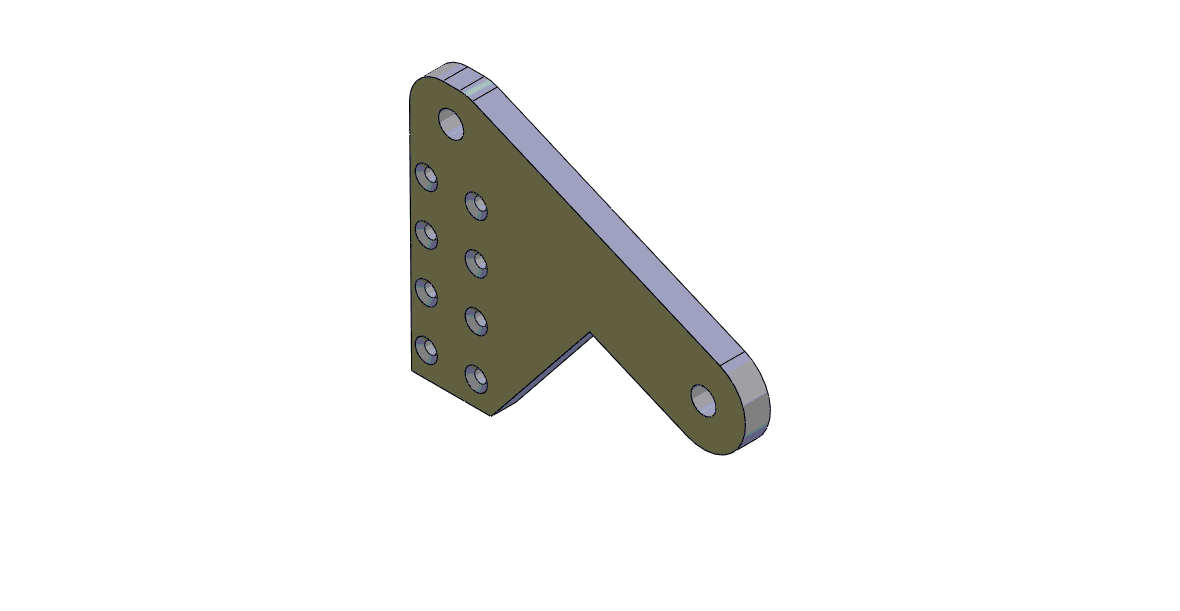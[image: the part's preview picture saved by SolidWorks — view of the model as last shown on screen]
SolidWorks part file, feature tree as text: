
SOLIDWORKS PART (.sldprt)
format: sldprt  version: not decoded by parser v0  size: 235,520 bytes
history: native  units: mm
features: sketch x5, hole x2, material x1, extrude x1 (+13 scaffold rows collapsed)
feature tree (22):
  scaffold x13  (default folders/planes/origin — collapsed)
  material  "Material <not specified>"
  sketch  "Sketch1"  dims[c1.D2=31.75mm c1.D6=9.525mm c2.D2=6.35mm c2.D3=12.7mm c2.D4=12.7mm c2.D5=~105.518712mm c2.D6=~326.848978mm c2.D7=101.6mm c2.D8=~102.576817mm c2.D9=~40.397386mm c2.D10=~59.997295mm c2.D11=~37.307113mm c2.D1=0.0mm]
  extrude  "Boss-Extrude1"  Depth=9.525mm
  hole  "3/8 (0.375) Diameter Hole1"  Diameter=9.525mm Depth=9.525mm
  sketch  "Sketch4"  dims[D1=12.7mm D2=~105.518712mm]
  sketch  "Sketch3"  dims[hole-wizard template sketch: 61 standard entries collapsed; hole parameters above]
  hole  "CSK for #8 Flat Head Machine Screw (100)1"  Diameter=4.4958mm Depth=9.525mm
  sketch  "Sketch5"
  sketch  "Sketch6"  dims[hole-wizard template sketch: 55 standard entries collapsed; hole parameters kept: c17.Thru Hole Depth=9.525mm c17.Near C'Sink Dia.=8.4328mm c17.D4=~3.666174mm c17.Near C'Sink Angle=100.0deg]
decode coverage: 7 of 8 modeling features carry decoded parameters
note: ~ marks probable driven/reference dimensions
note: suppression state not decoded; provenance and decode notes live in map.json
